# Revit family: Ahlsell_Кран_Шаровый_Бабочка
name_source: partatom
category: Арматура трубопроводов
revit_build: Autodesk Revit 2016 (Build: 20150220_1215(x64)
units: mm (PartAtom-declared; Revit-internal decimal feet)

## family parameters
Всегда вертикально = Нет
На основе рабочей плоскости = Нет
Общий = Нет
При загрузке вырезать с полостями = Нет
Размер круглого соединителя = Использовать диаметр
Тип детали = Клапан - Вставляется

## types (6) — shared parameters
ADSK_URL страницы изделия = http://www.ahlsell.ru
ADSK_Единица измерения = шт.
ADSK_Завод-изготовитель = Алсель
ADSK_Страна производства = AHLSELL_PEX – Испания, Китай
Толщина_Гайки = 10 мм

## per-type parameters (varying)
| type | ADSK_Диаметр условный | ADSK_Код изделия | ADSK_Масса_Текст | ВН_ВР | ВР_ВР | Высота_Бабочки | Высота_Вентиля | Длина_Бабочки | Длина_Крана | Тип_Бабочки | Ширина_Гайки |
| Кран шаровый бабочка ahlsell  DN 1/2" ВР-ВР | 15 мм | AHLBV12FFTHRB | 0.115 | Нет | Да | 32 мм | 16 мм | 48 мм | 46 мм | Бабочка : 1/2'' | 25 мм |
| Кран шаровый бабочка ahlsell  DN 3/4" ВР-ВР | 20 мм | AHLBV34FFTHRB | 0.165 | Нет | Да | 35 мм | 16 мм | 48 мм | 53 мм | Бабочка : 3/4'' | 30 мм |
| Кран шаровый бабочка ahlsell  DN 1" ВР-ВР | 25 мм | AHLBV1FFTHRB | 0.286 | Нет | Да | 46 мм | 21 мм | 64 мм | 62 мм | Бабочка : 1'' | 36 мм |
| Кран шаровый бабочка ahlsell  DN 1/2" НР-ВР | 15 мм | AHLBV12MFTHFB | 0.120 | Да | Нет | 32 мм | 16 мм | 48 мм | 46 мм | Бабочка : 1/2'' | 25 мм |
| Кран шаровый бабочка ahlsell  DN 3/4" НР-ВР | 20 мм | AHLBV34MFTHFB | 0.167 | Да | Нет | 35 мм | 16 мм | 48 мм | 53 мм | Бабочка : 3/4'' | 30 мм |
| Кран шаровый бабочка ahlsell  DN 1" НР-ВР | 25 мм | AHLBV1MFTHFB | 0.305 | Да | Нет | 46 мм | 21 мм | 64 мм | 62 мм | Бабочка : 1'' | 36 мм |

note: column(s) folded — value = type name in every type: ADSK_Наименование
